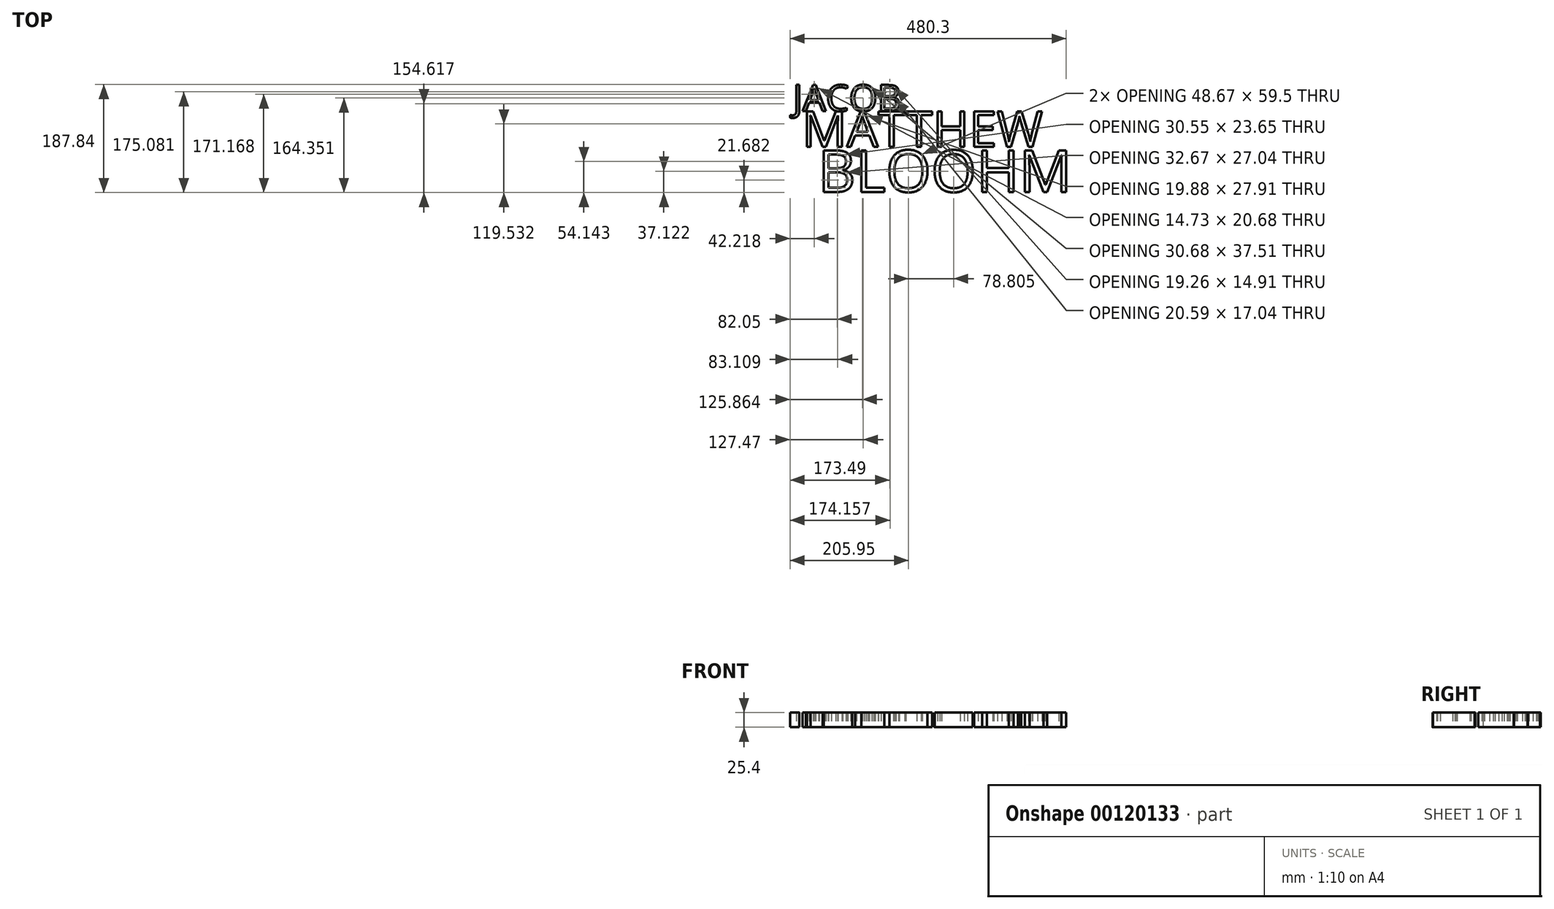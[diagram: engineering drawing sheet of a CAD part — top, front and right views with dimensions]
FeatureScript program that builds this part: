
annotation { "Feature Type Name" : "Feature", "Feature Type Description" : "" }
export const myFeature = defineFeature(function(context is Context, id is Id, definition is map)
    precondition{}
    {
        {
            var Q0;
            Q0=qCreatedBy(makeId("Top.planeOp"),FACE);
            var sketch = newSketch(context, id + "F0", { "sketchPlane" : qUnion([Q0])});
            skText(sketch, "E0", { "text": "JACOB\n", "fontName": "OpenSans-Regular.ttf"});
            const initialGuessF0  = {"E0": [0, 0, 1, 0, 0.04593]};
            skSetInitialGuess(sketch, initialGuessF0);
            skSolve(sketch);
        }
        {
            var Q0;
            Q0 = qSketchRegion(id + "F0", true);
            extrude(context, id + "F1", {"entities" : qUnion([Q0]), "depth" : 25.4 * mm});
        }
        {
            var Q0;
            Q0=qCreatedBy(makeId("Top.planeOp"),FACE);
            var sketch = newSketch(context, id + "F2", { "sketchPlane" : qUnion([Q0])});
            skText(sketch, "E1", { "text": "MATTHEW", "fontName": "OpenSans-Regular.ttf"});
            const initialGuessF2  = {"E1": [0.01592, -0.06197, 1, 0, 0.06197]};
            skSetInitialGuess(sketch, initialGuessF2);
            skSolve(sketch);
        }
        {
            var Q0;
            Q0 = qSketchRegion(id + "F2", true);
            extrude(context, id + "F3", {"entities" : qUnion([Q0]), "depth" : 25.4 * mm});
        }
        {
            var Q0;
            Q0=qCreatedBy(makeId("Top.planeOp"),FACE);
            var sketch = newSketch(context, id + "F4", { "sketchPlane" : qUnion([Q0])});
            skText(sketch, "E2", { "text": "BLOOHM", "fontName": "OpenSans-Regular.ttf"});
            const initialGuessF4  = {"E2": [0.04347, -0.14058, 1, 0, 0.07286]};
            skSetInitialGuess(sketch, initialGuessF4);
            skSolve(sketch);
        }
        {
            var Q0;
            Q0 = qSketchRegion(id + "F4", true);
            extrude(context, id + "F5", {"entities" : qUnion([Q0]), "depth" : 25.4 * mm});
        }
    });
